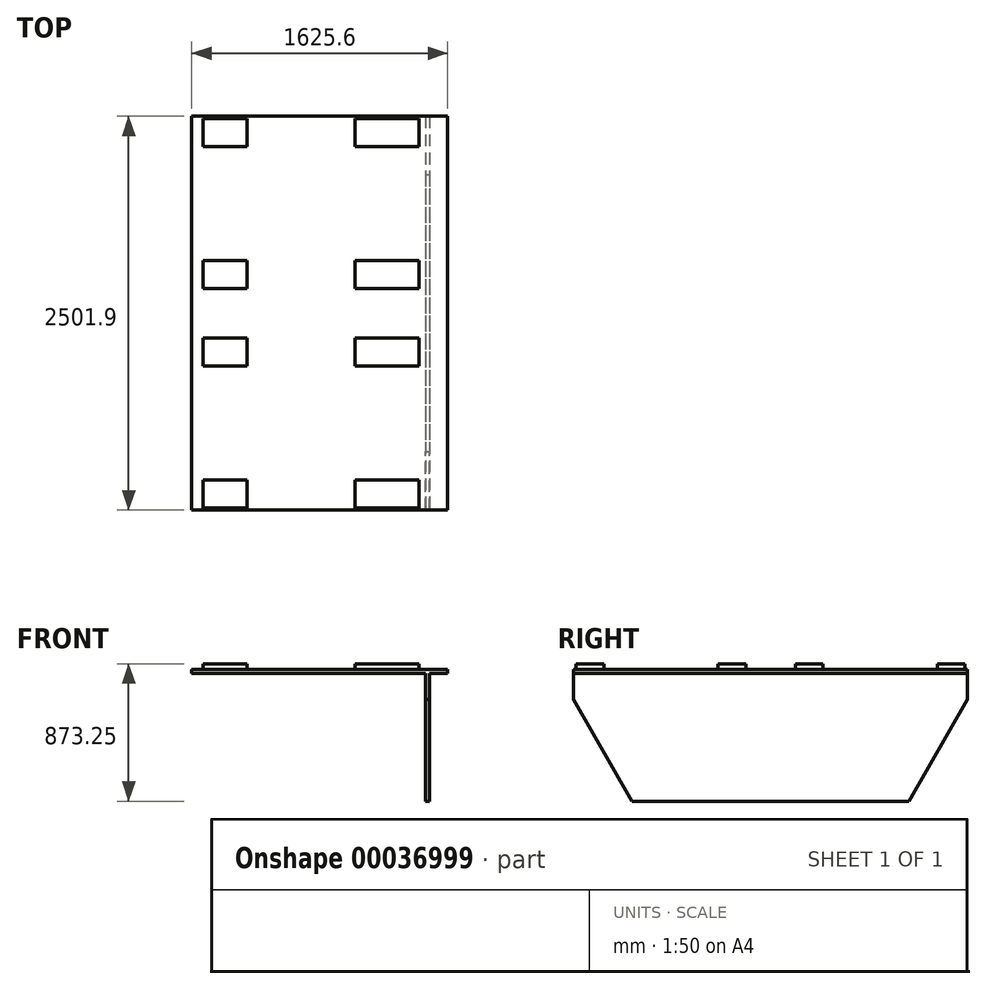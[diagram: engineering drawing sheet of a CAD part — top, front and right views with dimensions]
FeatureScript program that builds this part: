
annotation { "Feature Type Name" : "Feature", "Feature Type Description" : "" }
export const myFeature = defineFeature(function(context is Context, id is Id, definition is map)
    precondition{}
    {
        {
            var Q0;
            Q0=qCreatedBy(makeId("Top.planeOp"),FACE);
            var sketch = newSketch(context, id + "F0", { "sketchPlane" : qUnion([Q0])});
            skLineSegment(sketch, "E0.rect.bottom", {"start": v(-812.8, 1250.95) * mm, "end": v(812.8, 1250.95) * mm});
            skLineSegment(sketch, "E0.rect.top", {"start": v(-812.8, -1250.95) * mm, "end": v(812.8, -1250.95) * mm});
            skLineSegment(sketch, "E0.rect.left", {"start": v(-812.8, 1250.95) * mm, "end": v(-812.8, -1250.95) * mm});
            skLineSegment(sketch, "E0.rect.right", {"start": v(812.8, 1250.95) * mm, "end": v(812.8, -1250.95) * mm});
            skPoint(sketch, "E0.rect.middle", {"position": v(0, 0) * mm});
            skSolve(sketch);
        }
        {
            var Q0;
            Q0 = qSketchRegion(id + "F0", true);
            extrude(context, id + "F1", {"entities" : qUnion([Q0]), "depth" : 25.4 * mm});
        }
        {
            var Q0;
            Q0=makeQuery(id+"F1.opExtrude","CAP_FACE",FACE,{"disambiguationData":[OSD([sQuery(id+"F0.wireOp",EDGE,"E0.rect.bottom"),sQuery(id+"F0.wireOp",EDGE,"E0.rect.top"),sQuery(id+"F0.wireOp",EDGE,"E0.rect.left"),sQuery(id+"F0.wireOp",EDGE,"E0.rect.right")])],"isStart":false});
            var sketch = newSketch(context, id + "F2", { "sketchPlane" : qUnion([Q0])});
            skLineSegment(sketch, "E1.0", {"start": v(812.8, 1250.95) * mm, "end": v(812.8, -1250.95) * mm, "construction": true});
            skLineSegment(sketch, "E2.0", {"start": v(-741.43, -1235.2) * mm, "end": v(-462.03, -1235.2) * mm});
            skLineSegment(sketch, "E3.0", {"start": v(-741.43, -1057.4) * mm, "end": v(-462.03, -1057.4) * mm});
            skLineSegment(sketch, "E4.0", {"start": v(-741.43, -333.5) * mm, "end": v(-462.03, -333.5) * mm});
            skLineSegment(sketch, "E5.0", {"start": v(-741.43, -155.7) * mm, "end": v(-462.03, -155.7) * mm});
            skLineSegment(sketch, "E6.1", {"start": v(630.17, -155.7) * mm, "end": v(630.17, -333.5) * mm});
            skLineSegment(sketch, "E7.0", {"start": v(223.77, -155.7) * mm, "end": v(223.77, -333.5) * mm});
            skLineSegment(sketch, "E8.0", {"start": v(-462.03, 0) * mm, "end": v(-462.03, 0) * mm});
            skLineSegment(sketch, "E9.0", {"start": v(-741.43, -155.7) * mm, "end": v(-741.43, -333.5) * mm});
            skLineSegment(sketch, "E10", {"start": v(-812.8, 0) * mm, "end": v(812.8, 0) * mm, "construction": true});
            skPoint(sketch, "E10.endSnap0", {"position": v(-462.03, 0) * mm});
            skPoint(sketch, "E11.orphan", {"position": v(-462.03, 1235.2) * mm});
            skLineSegment(sketch, "E12.trimOffspring", {"start": v(-462.03, -155.7) * mm, "end": v(-462.03, -333.5) * mm});
            skLineSegment(sketch, "E13.trimOffspring", {"start": v(223.77, -333.5) * mm, "end": v(630.17, -333.5) * mm});
            skLineSegment(sketch, "E14.trimOffspring", {"start": v(223.77, -155.7) * mm, "end": v(630.17, -155.7) * mm});
            skLineSegment(sketch, "E15.trimOffspring", {"start": v(-462.03, -1057.4) * mm, "end": v(-462.03, -1235.2) * mm});
            skLineSegment(sketch, "E16.trimOffspring", {"start": v(-741.43, -1057.4) * mm, "end": v(-741.43, -1235.2) * mm});
            skLineSegment(sketch, "E17.trimOffspring", {"start": v(630.17, -1057.4) * mm, "end": v(630.17, -1235.2) * mm});
            skLineSegment(sketch, "E18.trimOffspring", {"start": v(223.77, -1057.4) * mm, "end": v(223.77, -1235.2) * mm});
            skLineSegment(sketch, "E19.trimOffspring", {"start": v(223.77, -1057.4) * mm, "end": v(630.17, -1057.4) * mm});
            skLineSegment(sketch, "E20.trimOffspring", {"start": v(223.77, -1235.2) * mm, "end": v(630.17, -1235.2) * mm});
            skPoint(sketch, "E21.0.start.orphan", {"position": v(-812.8, -1250.95) * mm});
            skLineSegment(sketch, "E22.MirrorCS", {"start": v(223.77, 1057.4) * mm, "end": v(223.77, 1235.2) * mm});
            skLineSegment(sketch, "E23.MirrorCS", {"start": v(630.17, 1057.4) * mm, "end": v(630.17, 1235.2) * mm});
            skLineSegment(sketch, "E24.MirrorCS", {"start": v(-741.43, 1057.4) * mm, "end": v(-741.43, 1235.2) * mm});
            skPoint(sketch, "E25.MirrorP", {"position": v(-812.8, 1250.95) * mm});
            skLineSegment(sketch, "E26.MirrorCS", {"start": v(223.77, 1235.2) * mm, "end": v(630.17, 1235.2) * mm});
            skLineSegment(sketch, "E27.MirrorCS", {"start": v(-741.43, 155.7) * mm, "end": v(-741.43, 333.5) * mm});
            skLineSegment(sketch, "E28.MirrorCS", {"start": v(223.77, 1057.4) * mm, "end": v(630.17, 1057.4) * mm});
            skLineSegment(sketch, "E29.MirrorCS", {"start": v(-462.03, 1057.4) * mm, "end": v(-462.03, 1235.2) * mm});
            skLineSegment(sketch, "E30.MirrorCS", {"start": v(223.77, 155.7) * mm, "end": v(223.77, 333.5) * mm});
            skLineSegment(sketch, "E31.MirrorCS", {"start": v(-741.43, 333.5) * mm, "end": v(-462.03, 333.5) * mm});
            skLineSegment(sketch, "E32.MirrorCS", {"start": v(223.77, 155.7) * mm, "end": v(630.17, 155.7) * mm});
            skLineSegment(sketch, "E33.MirrorCS", {"start": v(630.17, 155.7) * mm, "end": v(630.17, 333.5) * mm});
            skLineSegment(sketch, "E34.MirrorCS", {"start": v(223.77, 333.5) * mm, "end": v(630.17, 333.5) * mm});
            skLineSegment(sketch, "E35.MirrorCS", {"start": v(-741.43, 1057.4) * mm, "end": v(-462.03, 1057.4) * mm});
            skLineSegment(sketch, "E36.MirrorCS", {"start": v(-462.03, 155.7) * mm, "end": v(-462.03, 333.5) * mm});
            skLineSegment(sketch, "E37.MirrorCS", {"start": v(-741.43, 155.7) * mm, "end": v(-462.03, 155.7) * mm});
            skLineSegment(sketch, "E38.MirrorCS", {"start": v(-741.43, 1235.2) * mm, "end": v(-462.03, 1235.2) * mm});
            skSolve(sketch);
        }
        {
            var Q0;
            Q0 = qSketchRegion(id + "F2", true);
            extrude(context, id + "F3", {"entities" : qUnion([Q0]), "operationType" : NewBodyOperationType.ADD, "depth" : 35.05 * mm});
        }
        {
            var Q0;
            Q0=makeQuery(id+"F1.opExtrude","SWEPT_FACE",FACE,{"disambiguationData":[OSD([sQuery(id+"F0.wireOp",EDGE,"E0.rect.right")])]});
            cPlane(context, id + "F4", {"entities" : qUnion([Q0]), "cplaneType" : CPlaneType.OFFSET, "offset" : 114.3 * mm, "oppositeDirection" : true, "width" : 152.4 * mm, "height" : 152.4 * mm});
        }
        {
            var Q0;
            Q0=qCreatedBy(id+"F4.planeOp",FACE);
            var sketch = newSketch(context, id + "F5", { "sketchPlane" : qUnion([Q0])});
            skLineSegment(sketch, "E39.0", {"start": v(1250.95, 0) * mm, "end": v(-1250.95, 0) * mm});
            skLineSegment(sketch, "E40.0", {"start": v(1250.95, -812.8) * mm, "end": v(-1250.95, -812.8) * mm});
            skLineSegment(sketch, "E41.0", {"start": v(1250.95, -165.1) * mm, "end": v(-1250.95, -165.1) * mm});
            skLineSegment(sketch, "E42", {"start": v(0, -812.8) * mm, "end": v(0, 431.6) * mm, "construction": true});
            skLineSegment(sketch, "E43.0", {"start": v(-879.47, -812.8) * mm, "end": v(-879.47, 431.6) * mm, "construction": true});
            skLineSegment(sketch, "E44", {"start": v(-1250.95, 0) * mm, "end": v(-1250.95, -165.1) * mm});
            skLineSegment(sketch, "E45", {"start": v(-1250.95, -165.1) * mm, "end": v(-879.47, -812.8) * mm});
            skLineSegment(sketch, "E46.MirrorCS", {"start": v(1250.95, 0) * mm, "end": v(1250.95, -165.1) * mm});
            skLineSegment(sketch, "E47.MirrorCS", {"start": v(1250.95, -165.1) * mm, "end": v(879.48, -812.8) * mm});
            skSolve(sketch);
        }
        {
            var Q0;
            Q0 = qSketchRegion(id + "F5", true);
            extrude(context, id + "F6", {"entities" : qUnion([Q0]), "operationType" : NewBodyOperationType.ADD, "oppositeDirection" : true, "depth" : 25.4 * mm});
        }
    });
